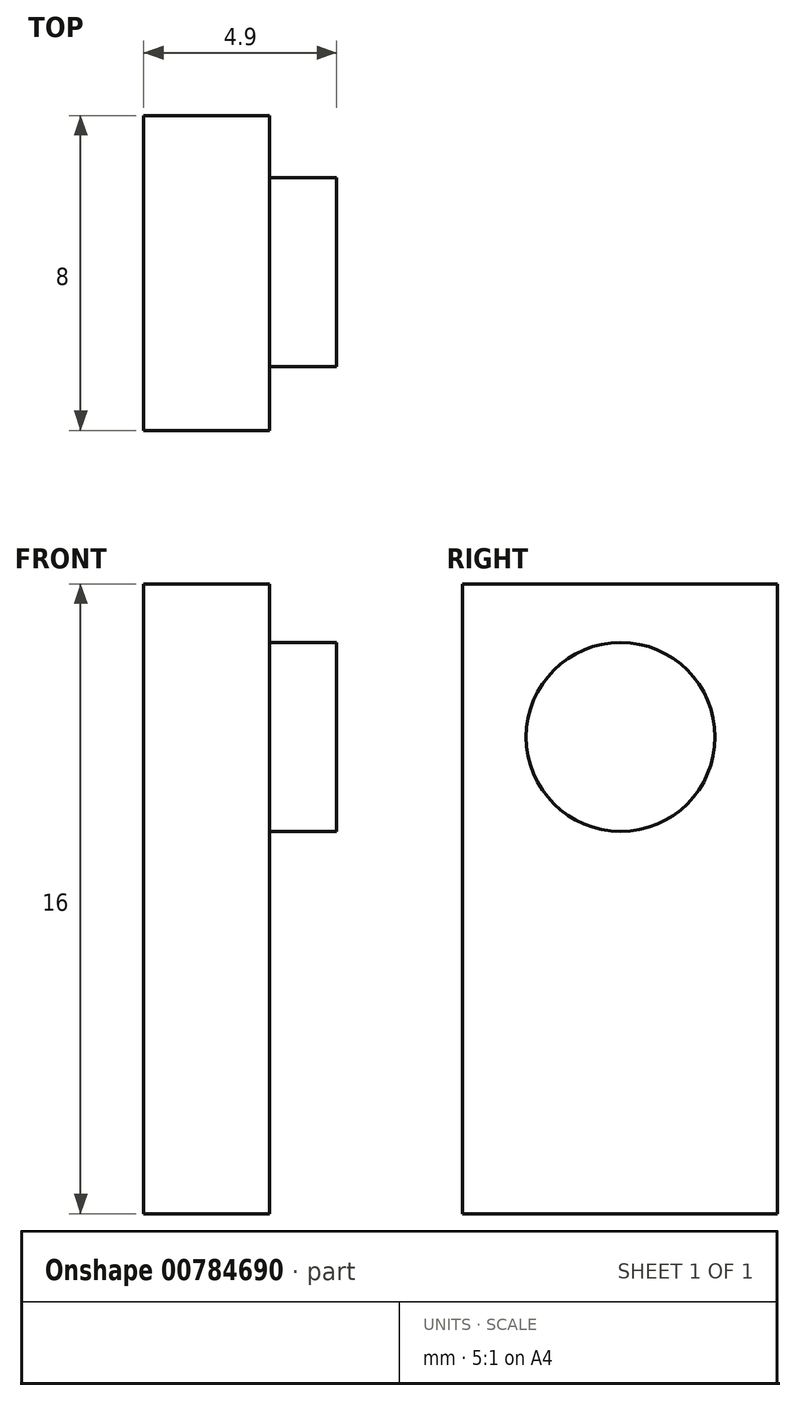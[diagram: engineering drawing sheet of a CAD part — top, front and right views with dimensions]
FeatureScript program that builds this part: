
annotation { "Feature Type Name" : "Feature", "Feature Type Description" : "" }
export const myFeature = defineFeature(function(context is Context, id is Id, definition is map)
    precondition{}
    {
        {
            var Q0;
            Q0=qCreatedBy(makeId("Right.planeOp"),FACE);
            var sketch = newSketch(context, id + "F0", { "sketchPlane" : qUnion([Q0])});
            skPoint(sketch, "E0.start.orphan", {"position": v(0, 0) * mm});
            skLineSegment(sketch, "E1", {"start": v(0, 0) * mm, "end": v(0, 16) * mm});
            skLineSegment(sketch, "E2", {"start": v(0, 16) * mm, "end": v(8, 16) * mm});
            skLineSegment(sketch, "E3", {"start": v(8, 16) * mm, "end": v(8, 0) * mm});
            skLineSegment(sketch, "E4", {"start": v(8, 0) * mm, "end": v(0, 0) * mm});
            skSolve(sketch);
        }
        {
            var Q0;
            Q0=makeQuery(id+"F0.imprint","IMPRINT",FACE,{"disambiguationData":[TD([[makeQuery(id+"F0.imprint","IMPRINT",EDGE,{"derivedFrom":sQuery(id+"F0.wireOp",EDGE,"E1")}),-1.0]])]});
            var Q1;
            Q1 = qSketchRegion(id + "F2", true);
            extrude(context, id + "F1", {"entities" : qUnion([Q0, Q1]), "depth" : 3.2 * mm, "offsetDistance" : 25 * mm});
        }
        {
            var Q0;
            Q0=makeQuery(id+"F1.opExtrude","CAP_FACE",FACE,{"disambiguationData":[OSD([sQuery(id+"F0.wireOp",EDGE,"E1"),sQuery(id+"F0.wireOp",EDGE,"E2"),sQuery(id+"F0.wireOp",EDGE,"E3"),sQuery(id+"F0.wireOp",EDGE,"E4")])],"isStart":false});
            var sketch = newSketch(context, id + "F2", { "sketchPlane" : qUnion([Q0])});
            skPoint(sketch, "E5", {"position": v(4.03, 8) * mm});
            skPoint(sketch, "E6.start.orphan", {"position": v(0, 8) * mm});
            skPoint(sketch, "E7.end.orphan", {"position": v(4, 0) * mm});
            skPoint(sketch, "E8", {"position": v(4.04, 9.71) * mm});
            skPoint(sketch, "E9", {"position": v(4.03, 6.31) * mm});
            skCircle(sketch, "E10", {"center": v(4.02, 12.11) * mm, "radius": 2.4 * mm});
            skLineSegment(sketch, "E11", {"start": v(4, 0) * mm, "end": v(4.03, 6.31) * mm});
            skLineSegment(sketch, "E12", {"start": v(4.03, 8) * mm, "end": v(4.03, 6.31) * mm});
            skLineSegment(sketch, "E13", {"start": v(4, 0) * mm, "end": v(4.07, 16) * mm});
            skCircle(sketch, "E14", {"center": v(4.02, 3.92) * mm, "radius": 2.4 * mm});
            skSolve(sketch);
        }
        {
            var Q0;
            {var subQ0=sQuery(id+"F2.wireOp",EDGE,"E13");var subQ1=sQuery(id+"F2.wireOp",EDGE,"E10");var subQ2=makeQuery(id+"F2.imprint","INTERSECT",VERTEX,{"disambiguationData":[OD(0.0)],"derivedFrom":[subQ1,subQ0]});Q0=makeQuery(id+"F2.imprint","IMPRINT",FACE,{"disambiguationData":[TD([[makeQuery(id+"F2.imprint","IMPRINT",EDGE,{"disambiguationData":[TD([[subQ2,1.0]])],"derivedFrom":subQ1}),1.0]])]});}
            var Q1;
            {var subQ0=sQuery(id+"F2.wireOp",EDGE,"E13");var subQ1=sQuery(id+"F2.wireOp",EDGE,"E10");var subQ2=makeQuery(id+"F2.imprint","INTERSECT",VERTEX,{"disambiguationData":[OD(0.0)],"derivedFrom":[subQ1,subQ0]});Q1=makeQuery(id+"F2.imprint","IMPRINT",FACE,{"disambiguationData":[TD([[makeQuery(id+"F2.imprint","IMPRINT",EDGE,{"disambiguationData":[TD([[subQ2,-1.0]])],"derivedFrom":subQ1}),1.0]])]});}
            var Q2;
            {var subQ0=sQuery(id+"F2.wireOp",EDGE,"E14");var subQ1=sQuery(id+"F2.wireOp",EDGE,"E13");var subQ2=makeQuery(id+"F2.imprint","INTERSECT",VERTEX,{"disambiguationData":[OD(0.0)],"derivedFrom":[subQ1,subQ0]});Q2=makeQuery(id+"F2.imprint","IMPRINT",FACE,{"disambiguationData":[TD([[makeQuery(id+"F2.imprint","IMPRINT",EDGE,{"disambiguationData":[TD([[subQ2,-1.0]])],"derivedFrom":subQ1}),-1.0]])]});}
            var Q3;
            {var subQ0=sQuery(id+"F2.wireOp",EDGE,"E14");var subQ1=sQuery(id+"F2.wireOp",EDGE,"E13");var subQ2=makeQuery(id+"F2.imprint","INTERSECT",VERTEX,{"disambiguationData":[OD(0.0)],"derivedFrom":[subQ1,subQ0]});Q3=makeQuery(id+"F2.imprint","IMPRINT",FACE,{"disambiguationData":[TD([[makeQuery(id+"F2.imprint","IMPRINT",EDGE,{"disambiguationData":[TD([[subQ2,-1.0]])],"derivedFrom":subQ1}),1.0]])]});}
            extrude(context, id + "F3", {"entities" : qUnion([Q0, Q1, Q2, Q3]), "operationType" : NewBodyOperationType.ADD, "depth" : 1.7 * mm, "offsetDistance" : 25 * mm});
        }
    });
